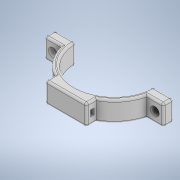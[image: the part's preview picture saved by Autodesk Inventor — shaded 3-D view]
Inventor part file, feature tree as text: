
AUTODESK INVENTOR PART (.ipt)
format: ipt  version: 2020 (Build 240168000, 168)  size: 270,848 bytes
history: native  units: in
note: dims shown in document units (in); Inventor stores cm internally (conversion verified against a paired STEP export)
features: sketch x6, extrude x5, plane x2, mirror x2, shell x1, hole x1, fillet x1, chamfer x1
ambient origin geometry x8: Origin, YZ Plane, XZ Plane, XY Plane, X Axis, Y Axis, Z Axis, Center Point
bodies: Solid1 (feature_tree)
feature tree (19):
  extrude  "Extrusion1"  Depth=0.1969in TaperAngle=0.0deg
  shell  "Shell1"  Thickness=0.1969in
  extrude  "Extrusion2"  [1 undecoded]
  plane  "Work Plane1"
  extrude  "Extrusion3"  Depth=0.3937in
  mirror  "Mirror1"
  hole  "Hole2"  [1 undecoded]
  mirror  "Mirror2"
  plane  "Work Plane2"
  extrude  "Extrusion4"  Depth=0.0984in TaperAngle=0.0deg
  fillet  "Fillet2"  Radius=0.0787in
  extrude  "Extrusion6"  Depth=0.0984in
  chamfer  "Chamfer3"  Distance=0.1969in
  sketch  "Sketch1"  dims[d0=3.3465in d1=0.7874in d2=0.0in d3=0.1969in]
  sketch  "Sketch2"  dims[d4=0.3937in d5=0.0in d6=-1.6732in]
  sketch  "Sketch3"  dims[d7=0.7874in d8=0.3937in]
  sketch  "Sketch5"  dims[d9=0.0787in d10=0.5906in d11=0.0in d12=0.0in]
  sketch  "Sketch6"  dims[d20=0.2165in d21=0.2362in d22=0.3346in d23=0.1969in d24=90.0deg d25=0.315in d26=0.8108in d27=1.5748in]
  sketch  "Sketch10"  dims[d28=1.5748in d29=0.2756in d30=0.0984in d31=0.0in d32=0.0in d43=0.0787in d47=0.0984in d48=0.1969in d49=0.0in d50=0.0in d51=0.0197in d52=0.0787in d53=45.0deg]
note: 2 required parameter values undecoded (feature->parameter linkage not recoverable at this tier; creation-order binding heuristic only, values carry confidence <= 0.55)
